# Revit family: 32-642-xx - Klone (Pendant)
name_source: partatom
category: Lighting Fixtures
revit_build: Autodesk Revit 2018 (Build: 20180423_1000(x64)
units: mm (PartAtom-declared; Revit-internal decimal feet)

## family parameters
Always vertical = Yes
Cut with Voids When Loaded = No
Host = Ceiling
Light Source = Yes
OmniClass Number = 23.80.70.11
OmniClass Title = Luminaries for Internal Lighting
Part Type = Normal
Room Calculation Point = No
Round Connector Dimension = Use Diameter
Shared = No

## types (4) — shared parameters
Assembly Code = --
Color Filter = 16777215
Description = --
Diffuser = Matte White Acrylic
Dimming Lamp Color Temperature Shift = <None>
Emit Shape Visible in Rendering = No
Emit from Rectangle Length = 40 "
Emit from Rectangle Width = 3 "
Input Voltage = 120V or 277V 50/60Hz
Keynote = LED array lamp
Lamp = LED Array
Manufacturer = Oxygen Lighting
Photometric Web File = 32-642 Klone.ies
Tilt Angle = 90.00°
Type Comments = LED Lighting Fixture
URL = www.oxygenlighting.com
Wattage Comments = 56.7W at 120V
zero-valued in all types: Cost

## per-type parameters (varying)
| type | Electrical Cable | Metal Finish |
| 32-642-15 - Klone | 15 - Black | 15 - Black |
| 32-642-16 - Klone | 16 - Gray | 16 - Gray |
| 32-642-20 - Klone | 16 - Gray | 20 - Polished Nickel |
| 32-642-24 - Klone | 16 - Gray | 24 - Satin Nickel |

note: column(s) folded — value = type name in every type: Model

## geometry (parser evidence)
native form markers: Extrusion x1, Sweep x6
no freeform markers — native parametric forms only
